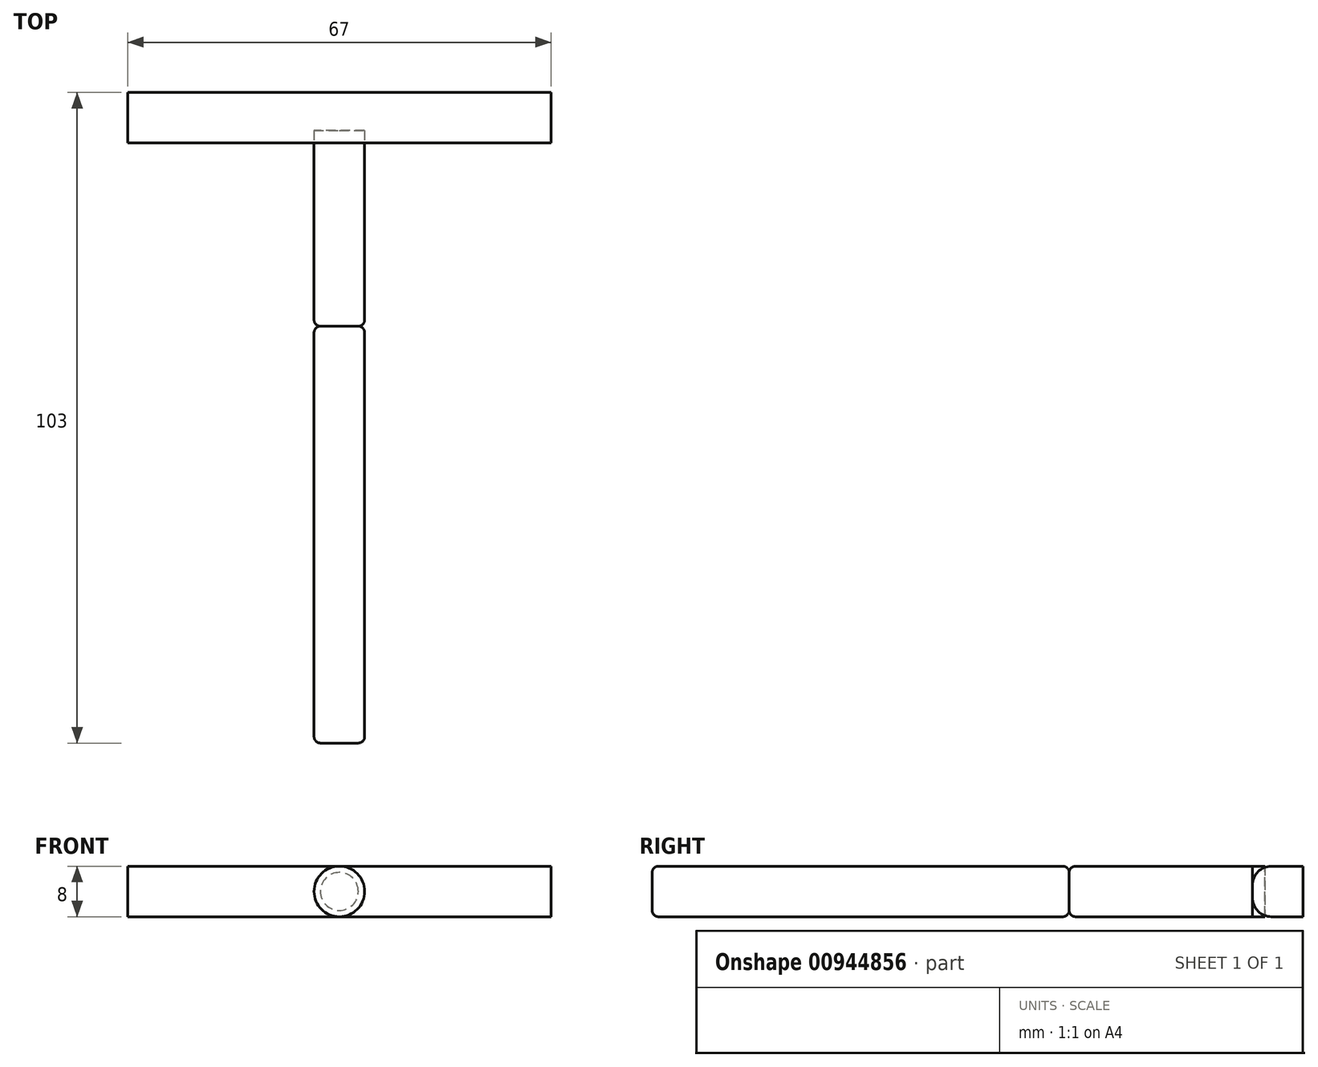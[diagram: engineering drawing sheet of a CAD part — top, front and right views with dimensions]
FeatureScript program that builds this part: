
annotation { "Feature Type Name" : "Feature", "Feature Type Description" : "" }
export const myFeature = defineFeature(function(context is Context, id is Id, definition is map)
    precondition{}
    {
        {
            var Q0;
            Q0=qCreatedBy(makeId("Top.planeOp"),FACE);
            var sketch = newSketch(context, id + "F0", { "sketchPlane" : qUnion([Q0])});
            skLineSegment(sketch, "E0.bottom", {"start": v(33.5, 4) * mm, "end": v(-33.5, 4) * mm});
            skLineSegment(sketch, "E0.top", {"start": v(33.5, -4) * mm, "end": v(-33.5, -4) * mm});
            skLineSegment(sketch, "E0.left", {"start": v(33.5, 4) * mm, "end": v(33.5, -4) * mm});
            skLineSegment(sketch, "E0.right", {"start": v(-33.5, 4) * mm, "end": v(-33.5, -4) * mm});
            skPoint(sketch, "E0.middle", {"position": v(0, 0) * mm});
            skLineSegment(sketch, "E1", {"start": v(0, -4) * mm, "end": v(0, -51.5) * mm});
            skLineSegment(sketch, "E2.bottom", {"start": v(-4, -4) * mm, "end": v(4, -4) * mm});
            skLineSegment(sketch, "E2.top", {"start": v(-4, -99) * mm, "end": v(4, -99) * mm});
            skLineSegment(sketch, "E2.left", {"start": v(-4, -4) * mm, "end": v(-4, -99) * mm});
            skLineSegment(sketch, "E2.right", {"start": v(4, -4) * mm, "end": v(4, -99) * mm});
            skPoint(sketch, "E2.middle", {"position": v(0, -51.5) * mm});
            skLineSegment(sketch, "E3", {"start": v(-4, -33) * mm, "end": v(4, -33) * mm});
            skLineSegment(sketch, "E4", {"start": v(0, -51.5) * mm, "end": v(0, -99) * mm});
            skLineSegment(sketch, "E5", {"start": v(0, -4) * mm, "end": v(0, 4) * mm});
            skLineSegment(sketch, "E6", {"start": v(0, 4) * mm, "end": v(4, 4) * mm});
            skLineSegment(sketch, "E7", {"start": v(4, 4) * mm, "end": v(4, -4) * mm});
            skLineSegment(sketch, "E8", {"start": v(-4, -4) * mm, "end": v(-4, 4) * mm});
            skLineSegment(sketch, "E9", {"start": v(-4, -2) * mm, "end": v(4, -2) * mm});
            skSolve(sketch);
        }
        {
            var Q0;
            {var subQ3=sQuery(id+"F0.wireOp",EDGE,"E2.right");var subQ5=sQuery(id+"F0.wireOp",EDGE,"E3");var subQ6=makeQuery(id+"F0.imprint","INTERSECT",VERTEX,{"derivedFrom":[subQ3,subQ5]});Q0=makeQuery(id+"F0.imprint","IMPRINT",FACE,{"disambiguationData":[TD([[makeQuery(id+"F0.imprint","IMPRINT",EDGE,{"disambiguationData":[TD([[subQ6,1.0]])],"derivedFrom":subQ5}),1.0]])]});}
            var Q1;
            Q1=sQuery(id+"F0.wireOp",EDGE,"E1");
            revolve(context, id + "F1", {"surfaceOperationType" : NewSurfaceOperationType.NEW, "entities" : qUnion([Q0]), "axis" : qUnion([Q1]), "revolveType" : RevolveType.FULL});
        }
        {
            var Q0;
            Q0=makeQuery(id+"F1.opRevolve","SWEPT_EDGE",EDGE,{"disambiguationData":[OSD([sQuery(id+"F0.wireOp",EDGE,"E2.right"),sQuery(id+"F0.wireOp",EDGE,"E3")])]});
            fillet(context, id + "F2", {"entities" : qUnion([Q0]), "radius" : 1 * mm, "tangentPropagation" : true, "allowEdgeOverflow" : false});
        }
        {
            var Q0;
            {var subQ0=sQuery(id+"F0.wireOp",EDGE,"E5");var subQ1=sQuery(id+"F0.wireOp",EDGE,"E0.bottom");var subQ2=makeQuery(id+"F0.imprint","INTERSECT",VERTEX,{"derivedFrom":[subQ1,subQ0]});var subQ5=sQuery(id+"F0.wireOp",EDGE,"E9");var subQ7=makeQuery(id+"F0.imprint","INTERSECT",VERTEX,{"derivedFrom":[subQ0,subQ5]});var subQ8=makeQuery(id+"F0.imprint","IMPRINT",EDGE,{"disambiguationData":[TD([[subQ7,-1.0]])],"derivedFrom":subQ5});Q0=qUnion([makeQuery(id+"F0.imprint","IMPRINT",FACE,{"disambiguationData":[TD([[subQ8,-1.0]])]}),makeQuery(id+"F0.imprint","IMPRINT",FACE,{"disambiguationData":[TD([[makeQuery(id+"F0.imprint","IMPRINT",EDGE,{"disambiguationData":[TD([[subQ2,1.0]])],"derivedFrom":subQ1}),1.0]])]})]);}
            var Q1;
            {var subQ0=sQuery(id+"F0.wireOp",EDGE,"E8");var subQ3=sQuery(id+"F0.wireOp",EDGE,"E5");var subQ5=sQuery(id+"F0.wireOp",EDGE,"E9");var subQ7=makeQuery(id+"F0.imprint","INTERSECT",VERTEX,{"derivedFrom":[subQ3,subQ5]});var subQ8=makeQuery(id+"F0.imprint","IMPRINT",EDGE,{"disambiguationData":[TD([[subQ7,1.0]])],"derivedFrom":subQ5});var subQ9=sQuery(id+"F0.wireOp",EDGE,"E0.bottom");var subQ10=makeQuery(id+"F0.imprint","INTERSECT",VERTEX,{"derivedFrom":[subQ9,subQ0]});Q1=qUnion([makeQuery(id+"F0.imprint","IMPRINT",FACE,{"disambiguationData":[TD([[makeQuery(id+"F0.imprint","IMPRINT",EDGE,{"disambiguationData":[TD([[subQ10,1.0]])],"derivedFrom":subQ9}),1.0]])]}),makeQuery(id+"F0.imprint","IMPRINT",FACE,{"disambiguationData":[TD([[subQ8,-1.0]])]})]);}
            var Q2;
            {var subQ4=sQuery(id+"F0.wireOp",EDGE,"E0.left");Q2=makeQuery(id+"F0.imprint","IMPRINT",FACE,{"disambiguationData":[TD([[makeQuery(id+"F0.imprint","IMPRINT",EDGE,{"derivedFrom":subQ4}),-1.0]])]});}
            var Q3;
            {var subQ0=sQuery(id+"F0.wireOp",EDGE,"E0.right");Q3=makeQuery(id+"F0.imprint","IMPRINT",FACE,{"disambiguationData":[TD([[makeQuery(id+"F0.imprint","IMPRINT",EDGE,{"derivedFrom":subQ0}),1.0]])]});}
            extrude(context, id + "F3", {"entities" : qUnion([Q0, Q1, Q2, Q3]), "endBound" : BoundingType.SYMMETRIC, "depth" : 8 * mm, "offsetDistance" : 25 * mm});
        }
        {
            var Q0;
            {var subQ7=sQuery(id+"F0.wireOp",EDGE,"E4");Q0=makeQuery(id+"F0.imprint","IMPRINT",FACE,{"disambiguationData":[TD([[makeQuery(id+"F0.imprint","IMPRINT",EDGE,{"derivedFrom":subQ7}),1.0]])]});}
            var Q1;
            Q1=sQuery(id+"F0.wireOp",EDGE,"E4");
            revolve(context, id + "F4", {"operationType" : NewBodyOperationType.ADD, "surfaceOperationType" : NewSurfaceOperationType.NEW, "entities" : qUnion([Q0]), "axis" : qUnion([Q1]), "revolveType" : RevolveType.FULL});
        }
        {
            var Q0;
            Q0=makeQuery(id+"F4.opRevolve","SWEPT_EDGE",EDGE,{"disambiguationData":[OSD([sQuery(id+"F0.wireOp",EDGE,"E2.right"),sQuery(id+"F0.wireOp",EDGE,"E3")])]});
            fillet(context, id + "F5", {"entities" : qUnion([Q0]), "radius" : 1 * mm, "tangentPropagation" : true, "allowEdgeOverflow" : false});
        }
        {
            var Q0;
            Q0=makeQuery(id+"F4.opRevolve","SWEPT_EDGE",EDGE,{"disambiguationData":[OSD([sQuery(id+"F0.wireOp",EDGE,"E2.top"),sQuery(id+"F0.wireOp",EDGE,"E2.right")])]});
            fillet(context, id + "F6", {"entities" : qUnion([Q0]), "radius" : 1 * mm, "tangentPropagation" : true, "allowEdgeOverflow" : false});
        }
        {
            var Q0;
            Q0=makeQuery(id+"F3.opExtrude","CAP_EDGE",EDGE,{"disambiguationData":[OSD([sQuery(id+"F0.wireOp",EDGE,"E0.top")])],"isStart":true});
            var Q1;
            Q1=makeQuery(id+"F3.opExtrude","CAP_EDGE",EDGE,{"disambiguationData":[OSD([sQuery(id+"F0.wireOp",EDGE,"E0.top")])],"isStart":false});
            fillet(context, id + "F7", {"entities" : qUnion([Q0, Q1]), "radius" : 3 * mm, "tangentPropagation" : true, "allowEdgeOverflow" : false});
        }
        {
            var Q0;
            {var subQ3=sQuery(id+"F0.wireOp",EDGE,"E5");var subQ5=sQuery(id+"F0.wireOp",EDGE,"E9");var subQ7=makeQuery(id+"F0.imprint","INTERSECT",VERTEX,{"derivedFrom":[subQ3,subQ5]});Q0=makeQuery(id+"F0.imprint","IMPRINT",FACE,{"disambiguationData":[TD([[makeQuery(id+"F0.imprint","IMPRINT",EDGE,{"disambiguationData":[TD([[subQ7,1.0]])],"derivedFrom":subQ5}),-1.0]])]});}
            var Q1;
            Q1=sQuery(id+"F0.wireOp",EDGE,"E5");
            revolve(context, id + "F8", {"surfaceOperationType" : NewSurfaceOperationType.NEW, "entities" : qUnion([Q0]), "axis" : qUnion([Q1]), "revolveType" : RevolveType.FULL});
        }
    });
